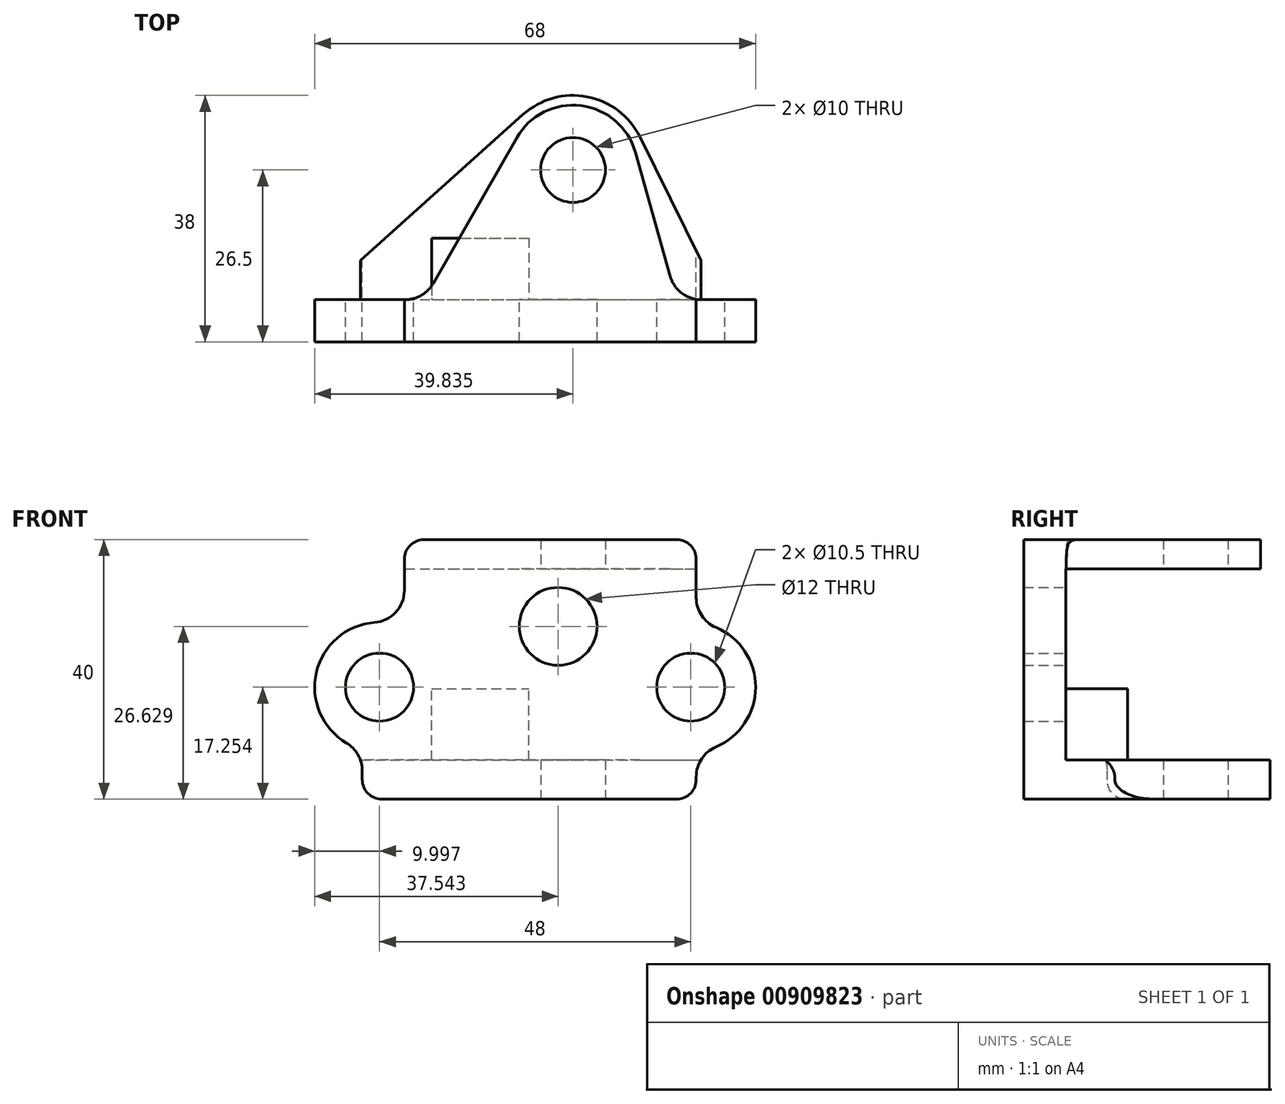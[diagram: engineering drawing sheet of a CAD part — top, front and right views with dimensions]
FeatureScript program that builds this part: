
annotation { "Feature Type Name" : "Feature", "Feature Type Description" : "" }
export const myFeature = defineFeature(function(context is Context, id is Id, definition is map)
    precondition{}
    {
        {
            var Q0;
            Q0=qCreatedBy(makeId("Front.planeOp"),FACE);
            var sketch = newSketch(context, id + "F0", { "sketchPlane" : qUnion([Q0])});
            skLineSegment(sketch, "E0.bottom", {"start": v(-8.21, 32.84) * mm, "end": v(30.79, 32.84) * mm});
            skLineSegment(sketch, "E1", {"start": v(-11.21, 29.84) * mm, "end": v(-11.21, 25.05) * mm});
            skLineSegment(sketch, "E2", {"start": v(33.79, 29.84) * mm, "end": v(33.79, 23.91) * mm});
            skCircle(sketch, "E3", {"center": v(-15.05, 10.1) * mm, "radius": 5.25 * mm});
            skCircle(sketch, "E4", {"center": v(32.95, 10.1) * mm, "radius": 5.25 * mm});
            skCircle(sketch, "E5", {"center": v(12.5, 19.47) * mm, "radius": 6 * mm});
            skArc(sketch, "E6", {"start": v(-15.83, 20.06) * mm, "mid": v(-24.8, 12.37) * mm, "end": v(-20.16, 1.5) * mm});
            skArc(sketch, "E7", {"start": v(36.84, 0.88) * mm, "mid": v(42.95, 10.1) * mm, "end": v(36.84, 19.3) * mm});
            skLineSegment(sketch, "E8.trimOffspring", {"start": v(33.79, -3.72) * mm, "end": v(33.79, -4.16) * mm});
            skLineSegment(sketch, "E9", {"start": v(30.79, -7.16) * mm, "end": v(-14.71, -7.16) * mm});
            skLineSegment(sketch, "E10", {"start": v(-17.71, -4.16) * mm, "end": v(-17.71, -2.8) * mm});
            skPoint(sketch, "E11.visualSharp", {"position": v(-11.21, 32.84) * mm});
            skArc(sketch, "E11.filletArc", {"start": v(-8.21, 32.84) * mm, "mid": v(-10.34, 31.96) * mm, "end": v(-11.21, 29.84) * mm});
            skPoint(sketch, "E12.visualSharp", {"position": v(33.79, 32.84) * mm});
            skArc(sketch, "E12.filletArc", {"start": v(33.79, 29.84) * mm, "mid": v(32.9, 31.96) * mm, "end": v(30.79, 32.84) * mm});
            skPoint(sketch, "E13.visualSharp", {"position": v(33.79, -7.16) * mm});
            skArc(sketch, "E13.filletArc", {"start": v(30.79, -7.16) * mm, "mid": v(32.9, -6.28) * mm, "end": v(33.79, -4.16) * mm});
            skPoint(sketch, "E14.visualSharp", {"position": v(-17.71, -7.16) * mm});
            skArc(sketch, "E14.filletArc", {"start": v(-17.71, -4.16) * mm, "mid": v(-16.84, -6.28) * mm, "end": v(-14.71, -7.16) * mm});
            skPoint(sketch, "E15.visualSharp", {"position": v(-11.21, 19.33) * mm});
            skArc(sketch, "E15.filletArc", {"start": v(-15.83, 20.06) * mm, "mid": v(-12.54, 21.65) * mm, "end": v(-11.21, 25.05) * mm});
            skPoint(sketch, "E16.visualSharp", {"position": v(-17.71, 0.45) * mm});
            skArc(sketch, "E16.filletArc", {"start": v(-17.71, -2.8) * mm, "mid": v(-18.37, -0.33) * mm, "end": v(-20.16, 1.5) * mm});
            skPoint(sketch, "E17.visualSharp", {"position": v(33.79, 20.06) * mm});
            skArc(sketch, "E17.filletArc", {"start": v(33.79, 23.91) * mm, "mid": v(34.62, 21.15) * mm, "end": v(36.84, 19.3) * mm});
            skPoint(sketch, "E18.visualSharp", {"position": v(33.79, 0.13) * mm});
            skArc(sketch, "E18.filletArc", {"start": v(36.84, 0.88) * mm, "mid": v(34.62, -0.96) * mm, "end": v(33.79, -3.72) * mm});
            skSolve(sketch);
        }
        {
            var Q0;
            Q0=makeQuery(id+"F0.imprint","IMPRINT",FACE,{"disambiguationData":[TD([[makeQuery(id+"F0.imprint","IMPRINT",EDGE,{"derivedFrom":sQuery(id+"F0.wireOp",EDGE,"E0.bottom")}),-1.0]])]});
            extrude(context, id + "F1", {"entities" : qUnion([Q0]), "depth" : 40 * mm, "offsetDistance" : 25 * mm});
        }
        {
            var Q0;
            Q0=qCreatedBy(makeId("Right.planeOp"),FACE);
            var sketch = newSketch(context, id + "F2", { "sketchPlane" : qUnion([Q0])});
            skLineSegment(sketch, "E19.bottom", {"start": v(16.5, -1.16) * mm, "end": v(-33.5, -1.16) * mm});
            skLineSegment(sketch, "E19.top", {"start": v(16.5, 28.34) * mm, "end": v(-33.5, 28.34) * mm});
            skLineSegment(sketch, "E19.left", {"start": v(16.5, -1.16) * mm, "end": v(16.5, 28.34) * mm});
            skLineSegment(sketch, "E19.right", {"start": v(-33.5, -1.16) * mm, "end": v(-33.5, 28.34) * mm});
            skSolve(sketch);
        }
        {
            var Q0;
            Q0=makeQuery(id+"F2.imprint","IMPRINT",FACE,{"disambiguationData":[TD([[makeQuery(id+"F2.imprint","IMPRINT",EDGE,{"derivedFrom":sQuery(id+"F2.wireOp",EDGE,"E19.bottom")}),-1.0]])]});
            extrude(context, id + "F3", {"entities" : qUnion([Q0]), "operationType" : NewBodyOperationType.REMOVE, "oppositeDirection" : true, "depth" : 100 * mm, "offsetDistance" : 25 * mm});
        }
        {
            var Q0;
            Q0 = qSketchRegion(id + "F2", true);
            extrude(context, id + "F4", {"entities" : qUnion([Q0]), "operationType" : NewBodyOperationType.REMOVE, "depth" : 100 * mm, "offsetDistance" : 25 * mm});
        }
        {
            var Q0;
            Q0=makeQuery(id+"F1.opExtrude","SWEPT_FACE",FACE,{"disambiguationData":[OSD([sQuery(id+"F0.wireOp",EDGE,"E9")])]});
            var sketch = newSketch(context, id + "F5", { "sketchPlane" : qUnion([Q0])});
            skCircle(sketch, "E20", {"center": v(14.79, 13.5) * mm, "radius": 5 * mm});
            skSolve(sketch);
        }
        {
            var Q0;
            Q0=makeQuery(id+"F5.imprint","IMPRINT",FACE,{"disambiguationData":[TD([[makeQuery(id+"F5.imprint","IMPRINT",EDGE,{"derivedFrom":sQuery(id+"F5.wireOp",EDGE,"E20")}),1.0]])]});
            extrude(context, id + "F6", {"entities" : qUnion([Q0]), "operationType" : NewBodyOperationType.REMOVE, "oppositeDirection" : true, "depth" : 50 * mm, "offsetDistance" : 25 * mm});
        }
        {
            var Q0;
            Q0=makeQuery(id+"F1.opExtrude","SWEPT_FACE",FACE,{"disambiguationData":[OSD([sQuery(id+"F0.wireOp",EDGE,"E9")])]});
            var sketch = newSketch(context, id + "F7", { "sketchPlane" : qUnion([Q0])});
            skArc(sketch, "E21", {"start": v(7.11, 4.93) * mm, "mid": v(16.96, 2.2) * mm, "end": v(25.1, 8.4) * mm});
            skLineSegment(sketch, "E22", {"start": v(34.53, 27.5) * mm, "end": v(44.91, 27.5) * mm});
            skLineSegment(sketch, "E23", {"start": v(44.91, 27.5) * mm, "end": v(44.91, -4.18) * mm});
            skLineSegment(sketch, "E24", {"start": v(44.91, -4.18) * mm, "end": v(-24.33, -4.18) * mm});
            skLineSegment(sketch, "E25", {"start": v(-24.33, -4.18) * mm, "end": v(-24.33, 27.5) * mm});
            skLineSegment(sketch, "E26", {"start": v(-24.33, 27.5) * mm, "end": v(-18.08, 27.5) * mm});
            skLineSegment(sketch, "E27", {"start": v(34.53, 27.5) * mm, "end": v(25.1, 8.4) * mm});
            skLineSegment(sketch, "E28", {"start": v(-18.08, 27.5) * mm, "end": v(7.11, 4.93) * mm});
            skPoint(sketch, "E29.orphan", {"position": v(30.79, 27.5) * mm});
            skSolve(sketch);
        }
        {
            var Q0;
            {var subQ1=sQuery(id+"F7.wireOp",EDGE,"E21");Q0=makeQuery(id+"F7.imprint","IMPRINT",FACE,{"disambiguationData":[TD([[makeQuery(id+"F7.imprint","IMPRINT",EDGE,{"derivedFrom":subQ1}),-1.0]])]});}
            var Q1;
            {var subQ5=sQuery(id+"F7.wireOp",EDGE,"E22");Q1=makeQuery(id+"F7.imprint","IMPRINT",FACE,{"disambiguationData":[TD([[makeQuery(id+"F7.imprint","IMPRINT",EDGE,{"derivedFrom":subQ5}),-1.0]])]});}
            extrude(context, id + "F8", {"entities" : qUnion([Q0, Q1]), "operationType" : NewBodyOperationType.REMOVE, "oppositeDirection" : true, "depth" : 15 * mm, "offsetDistance" : 25 * mm});
        }
        {
            var Q0;
            Q0=makeQuery(id+"F1.opExtrude","SWEPT_FACE",FACE,{"disambiguationData":[OSD([sQuery(id+"F0.wireOp",EDGE,"E0.bottom")])]});
            var sketch = newSketch(context, id + "F9", { "sketchPlane" : qUnion([Q0])});
            skArc(sketch, "E30", {"start": v(24.41, -10.8) * mm, "mid": v(16.02, -3.58) * mm, "end": v(6.11, -8.52) * mm});
            skLineSegment(sketch, "E31", {"start": v(-11.11, -33.5) * mm, "end": v(-31.9, -33.5) * mm});
            skLineSegment(sketch, "E32", {"start": v(34.58, -33.5) * mm, "end": v(56, -33.5) * mm});
            skLineSegment(sketch, "E33", {"start": v(-6.77, -30.99) * mm, "end": v(6.11, -8.52) * mm});
            skLineSegment(sketch, "E34", {"start": v(29.76, -29.85) * mm, "end": v(24.41, -10.8) * mm});
            skPoint(sketch, "E35.visualSharp", {"position": v(-8.21, -33.5) * mm});
            skArc(sketch, "E35.filletArc", {"start": v(-11.11, -33.5) * mm, "mid": v(-8.6, -32.83) * mm, "end": v(-6.77, -30.99) * mm});
            skPoint(sketch, "E36.visualSharp", {"position": v(30.79, -33.5) * mm});
            skArc(sketch, "E36.filletArc", {"start": v(29.76, -29.85) * mm, "mid": v(31.55, -32.48) * mm, "end": v(34.58, -33.5) * mm});
            skLineSegment(sketch, "E37", {"start": v(-31.9, -33.5) * mm, "end": v(-12.64, 6.8) * mm});
            skLineSegment(sketch, "E38", {"start": v(-12.64, 6.8) * mm, "end": v(49.12, 6.8) * mm});
            skLineSegment(sketch, "E39", {"start": v(49.12, 6.8) * mm, "end": v(56, -33.5) * mm});
            skSolve(sketch);
        }
        {
            var Q0;
            Q0=makeQuery(id+"F9.imprint","IMPRINT",FACE,{"disambiguationData":[TD([[makeQuery(id+"F9.imprint","IMPRINT",EDGE,{"derivedFrom":sQuery(id+"F9.wireOp",EDGE,"E30")}),-1.0]])]});
            var Q1;
            {var subQ6=sQuery(id+"F9.wireOp",EDGE,"E31");Q1=makeQuery(id+"F9.imprint","IMPRINT",FACE,{"disambiguationData":[TD([[makeQuery(id+"F9.imprint","IMPRINT",EDGE,{"derivedFrom":subQ6}),-1.0]])]});}
            extrude(context, id + "F10", {"entities" : qUnion([Q0, Q1]), "operationType" : NewBodyOperationType.REMOVE, "oppositeDirection" : true, "depth" : 15 * mm, "offsetDistance" : 25 * mm});
        }
        {
            var Q0;
            {var subQ0=sQuery(id+"F2.wireOp",EDGE,"E19.right");Q0=makeQuery(id+"F10.boolean.opBoolean","MERGE",FACE,{"derivedFrom":[makeQuery(id+"F4.boolean.opBoolean","MERGE",FACE,{"derivedFrom":[makeQuery(id+"F3.boolean.opBoolean","COPY",FACE,{"derivedFrom":makeQuery(id+"F3.opExtrude","SWEPT_FACE",FACE,{"disambiguationData":[OSD([subQ0])]})})],"fromTools":[makeQuery(id+"F4.opExtrude","SWEPT_FACE",FACE,{"disambiguationData":[OSD([subQ0])]})]})],"fromTools":[makeQuery(id+"F10.opExtrude","SWEPT_FACE",FACE,{"disambiguationData":[OSD([sQuery(id+"F9.wireOp",EDGE,"E31")])]})]});}
            var sketch = newSketch(context, id + "F11", { "sketchPlane" : qUnion([Q0])});
            skLineSegment(sketch, "E40.bottom", {"start": v(7, -1.16) * mm, "end": v(-8, -1.16) * mm});
            skLineSegment(sketch, "E40.top", {"start": v(7, 9.84) * mm, "end": v(-8, 9.84) * mm});
            skLineSegment(sketch, "E40.left", {"start": v(7, -1.16) * mm, "end": v(7, 9.84) * mm});
            skLineSegment(sketch, "E40.right", {"start": v(-8, -1.16) * mm, "end": v(-8, 9.84) * mm});
            skSolve(sketch);
        }
        {
            var Q0;
            Q0=makeQuery(id+"F11.imprint","IMPRINT",FACE,{"disambiguationData":[TD([[makeQuery(id+"F11.imprint","IMPRINT",EDGE,{"derivedFrom":sQuery(id+"F11.wireOp",EDGE,"E40.bottom")}),-1.0]])]});
            extrude(context, id + "F12", {"entities" : qUnion([Q0]), "operationType" : NewBodyOperationType.ADD, "depth" : 9.5 * mm, "offsetDistance" : 25 * mm});
        }
    });
